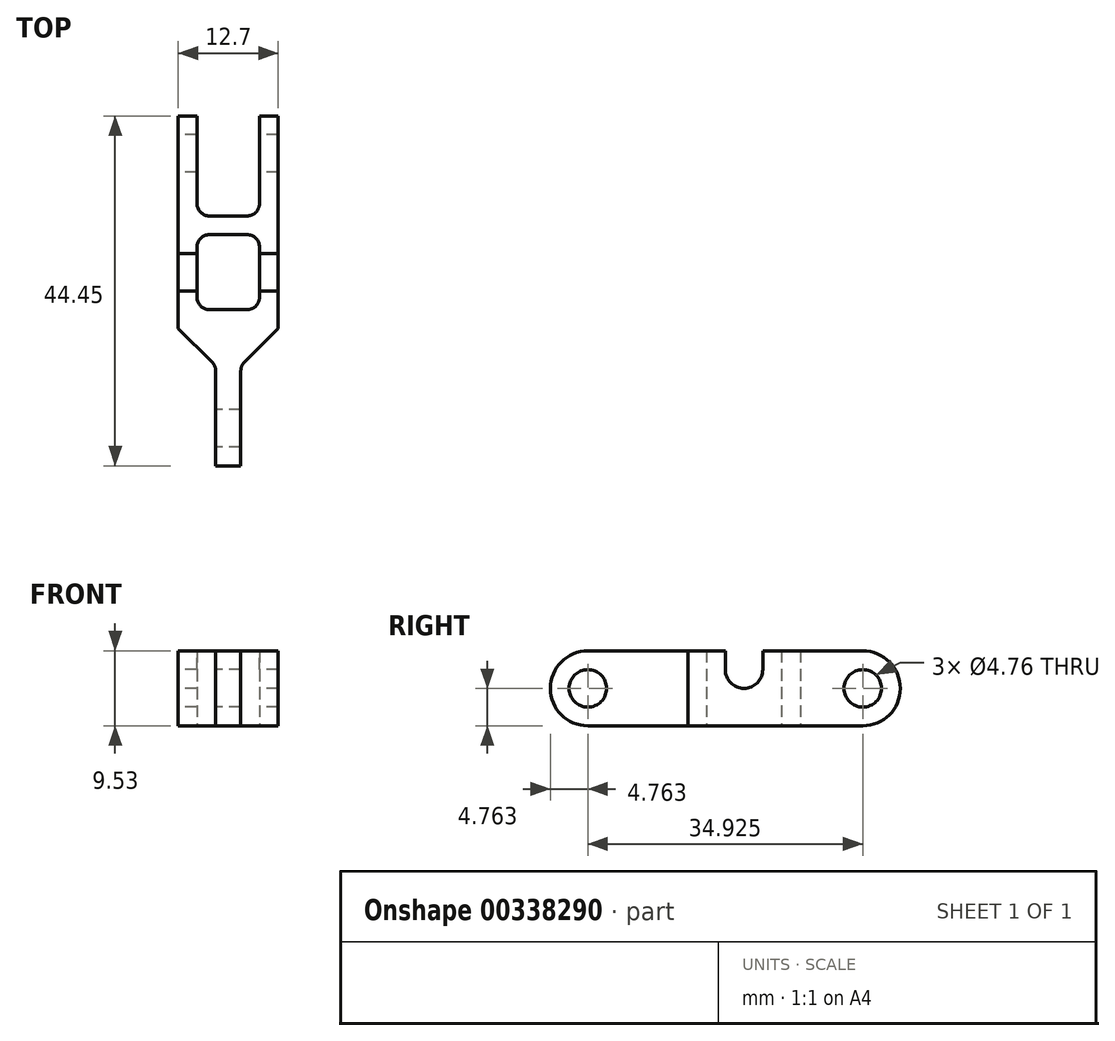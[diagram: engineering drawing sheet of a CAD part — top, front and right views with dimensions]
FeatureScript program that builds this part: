
annotation { "Feature Type Name" : "Feature", "Feature Type Description" : "" }
export const myFeature = defineFeature(function(context is Context, id is Id, definition is map)
    precondition{}
    {
        {
            var Q0;
            Q0=qCreatedBy(makeId("Top.planeOp"),FACE);
            var sketch = newSketch(context, id + "F0", { "sketchPlane" : qUnion([Q0])});
            skLineSegment(sketch, "E0.bottom", {"start": v(0, 0) * mm, "end": v(3.17, 0) * mm});
            skLineSegment(sketch, "E0.top", {"start": v(0, 12.7) * mm, "end": v(3.17, 12.7) * mm, "construction": true});
            skLineSegment(sketch, "E0.left", {"start": v(0, 0) * mm, "end": v(0, 12.7) * mm});
            skLineSegment(sketch, "E0.right", {"start": v(3.18, 0) * mm, "end": v(3.18, 12.7) * mm});
            skLineSegment(sketch, "E1", {"start": v(0, 12.7) * mm, "end": v(-4.76, 17.46) * mm});
            skLineSegment(sketch, "E2", {"start": v(3.17, 12.7) * mm, "end": v(7.94, 17.46) * mm});
            skLineSegment(sketch, "E3.bottom", {"start": v(-2.38, 29.37) * mm, "end": v(5.56, 29.37) * mm});
            skLineSegment(sketch, "E3.top", {"start": v(-2.38, 19.84) * mm, "end": v(5.56, 19.84) * mm});
            skLineSegment(sketch, "E3.left", {"start": v(-2.38, 29.37) * mm, "end": v(-2.38, 19.84) * mm});
            skLineSegment(sketch, "E3.right", {"start": v(5.56, 29.37) * mm, "end": v(5.56, 19.84) * mm});
            skLineSegment(sketch, "E4", {"start": v(1.59, 19.84) * mm, "end": v(1.59, 12.7) * mm, "construction": true});
            skLineSegment(sketch, "E5", {"start": v(1.59, 29.37) * mm, "end": v(1.59, 31.75) * mm});
            skLineSegment(sketch, "E6.bottom", {"start": v(-2.38, 31.75) * mm, "end": v(5.56, 31.75) * mm});
            skLineSegment(sketch, "E6.top", {"start": v(-2.38, 44.45) * mm, "end": v(5.56, 44.45) * mm, "construction": true});
            skLineSegment(sketch, "E6.left", {"start": v(-2.38, 31.75) * mm, "end": v(-2.38, 44.45) * mm});
            skLineSegment(sketch, "E6.right", {"start": v(5.56, 31.75) * mm, "end": v(5.56, 44.45) * mm});
            skLineSegment(sketch, "E7", {"start": v(-4.76, 17.46) * mm, "end": v(-4.76, 44.45) * mm});
            skLineSegment(sketch, "E8", {"start": v(-4.76, 44.45) * mm, "end": v(-2.38, 44.45) * mm});
            skLineSegment(sketch, "E9", {"start": v(5.56, 44.45) * mm, "end": v(7.94, 44.45) * mm});
            skLineSegment(sketch, "E10", {"start": v(7.94, 44.45) * mm, "end": v(7.94, 17.46) * mm});
            skSolve(sketch);
        }
        {
            var Q0;
            Q0 = qSketchRegion(id + "F0", true);
            extrude(context, id + "F1", {"entities" : qUnion([Q0]), "depth" : 9.52 * mm});
        }
        {
            var Q0;
            Q0=makeQuery(id+"F1.opExtrude","SWEPT_EDGE",EDGE,{"disambiguationData":[OSD([sQuery(id+"F0.wireOp",EDGE,"E6.bottom"),sQuery(id+"F0.wireOp",EDGE,"E6.left")])]});
            var Q1;
            Q1=makeQuery(id+"F1.opExtrude","SWEPT_EDGE",EDGE,{"disambiguationData":[OSD([sQuery(id+"F0.wireOp",EDGE,"E6.bottom"),sQuery(id+"F0.wireOp",EDGE,"E6.right")])]});
            var Q2;
            Q2=makeQuery(id+"F1.opExtrude","SWEPT_EDGE",EDGE,{"disambiguationData":[OSD([sQuery(id+"F0.wireOp",EDGE,"E3.bottom"),sQuery(id+"F0.wireOp",EDGE,"E3.right")])]});
            var Q3;
            Q3=makeQuery(id+"F1.opExtrude","SWEPT_EDGE",EDGE,{"disambiguationData":[OSD([sQuery(id+"F0.wireOp",EDGE,"E3.bottom"),sQuery(id+"F0.wireOp",EDGE,"E3.left")])]});
            var Q4;
            Q4=makeQuery(id+"F1.opExtrude","SWEPT_EDGE",EDGE,{"disambiguationData":[OSD([sQuery(id+"F0.wireOp",EDGE,"E3.top"),sQuery(id+"F0.wireOp",EDGE,"E3.left")])]});
            var Q5;
            Q5=makeQuery(id+"F1.opExtrude","SWEPT_EDGE",EDGE,{"disambiguationData":[OSD([sQuery(id+"F0.wireOp",EDGE,"E3.top"),sQuery(id+"F0.wireOp",EDGE,"E3.right")])]});
            var Q6;
            Q6=makeQuery(id+"F1.opExtrude","SWEPT_EDGE",EDGE,{"disambiguationData":[OSD([sQuery(id+"F0.wireOp",EDGE,"E0.left"),sQuery(id+"F0.wireOp",EDGE,"E1")])]});
            var Q7;
            Q7=makeQuery(id+"F1.opExtrude","SWEPT_EDGE",EDGE,{"disambiguationData":[OSD([sQuery(id+"F0.wireOp",EDGE,"E0.right"),sQuery(id+"F0.wireOp",EDGE,"E2")])]});
            fillet(context, id + "F2", {"entities" : qUnion([Q0, Q1, Q2, Q3, Q4, Q5, Q6, Q7]), "radius" : 1.59 * mm, "tangentPropagation" : true, "allowEdgeOverflow" : false});
        }
        {
            var Q0;
            Q0=makeQuery(id+"F1.opExtrude","CAP_EDGE",EDGE,{"disambiguationData":[OSD([sQuery(id+"F0.wireOp",EDGE,"E0.bottom")])],"isStart":false});
            var Q1;
            Q1=makeQuery(id+"F1.opExtrude","CAP_EDGE",EDGE,{"disambiguationData":[OSD([sQuery(id+"F0.wireOp",EDGE,"E0.bottom")])],"isStart":true});
            var Q2;
            Q2=makeQuery(id+"F1.opExtrude","CAP_EDGE",EDGE,{"disambiguationData":[OSD([sQuery(id+"F0.wireOp",EDGE,"E8")])],"isStart":false});
            var Q3;
            Q3=makeQuery(id+"F1.opExtrude","CAP_EDGE",EDGE,{"disambiguationData":[OSD([sQuery(id+"F0.wireOp",EDGE,"E8")])],"isStart":true});
            var Q4;
            Q4=makeQuery(id+"F1.opExtrude","CAP_EDGE",EDGE,{"disambiguationData":[OSD([sQuery(id+"F0.wireOp",EDGE,"E9")])],"isStart":false});
            var Q5;
            Q5=makeQuery(id+"F1.opExtrude","CAP_EDGE",EDGE,{"disambiguationData":[OSD([sQuery(id+"F0.wireOp",EDGE,"E9")])],"isStart":true});
            fillet(context, id + "F3", {"entities" : qUnion([Q0, Q1, Q2, Q3, Q4, Q5]), "radius" : 4.76 * mm, "tangentPropagation" : true, "allowEdgeOverflow" : false});
        }
        {
            var Q0;
            Q0=makeQuery(id+"F1.opExtrude","SWEPT_FACE",FACE,{"disambiguationData":[OSD([sQuery(id+"F0.wireOp",EDGE,"E7")])]});
            var sketch = newSketch(context, id + "F4", { "sketchPlane" : qUnion([Q0])});
            skCircle(sketch, "E11", {"center": v(-39.69, 4.76) * mm, "radius": 2.38 * mm});
            skCircle(sketch, "E12", {"center": v(-4.76, 4.76) * mm, "radius": 2.38 * mm});
            skLineSegment(sketch, "E13.bottom", {"start": v(-26.99, 9.53) * mm, "end": v(-22.23, 9.53) * mm});
            skLineSegment(sketch, "E13.top", {"start": v(-26.99, 7.14) * mm, "end": v(-22.23, 7.14) * mm, "construction": true});
            skLineSegment(sketch, "E13.left", {"start": v(-26.99, 9.52) * mm, "end": v(-26.99, 7.14) * mm});
            skLineSegment(sketch, "E13.right", {"start": v(-22.23, 9.53) * mm, "end": v(-22.23, 7.14) * mm});
            skArc(sketch, "E14", {"start": v(-26.99, 7.14) * mm, "mid": v(-24.6, 4.76) * mm, "end": v(-22.23, 7.14) * mm});
            skLineSegment(sketch, "E15", {"start": v(-24.6, 9.53) * mm, "end": v(-24.6, 4.76) * mm, "construction": true});
            skLineSegment(sketch, "E16", {"start": v(-24.6, 4.76) * mm, "end": v(-24.6, 0) * mm, "construction": true});
            skSolve(sketch);
        }
        {
            var Q0;
            Q0 = qSketchRegion(id + "F4", true);
            var Q1;
            Q1=makeQuery(id+"F1.opExtrude","SWEPT_FACE",FACE,{"disambiguationData":[OSD([sQuery(id+"F0.wireOp",EDGE,"E10")])]});
            extrude(context, id + "F5", {"entities" : qUnion([Q0]), "operationType" : NewBodyOperationType.REMOVE, "endBound" : BoundingType.UP_TO_SURFACE, "oppositeDirection" : true, "endBoundEntityFace" : qUnion([Q1]), "depth" : 25.4 * mm});
        }
    });
